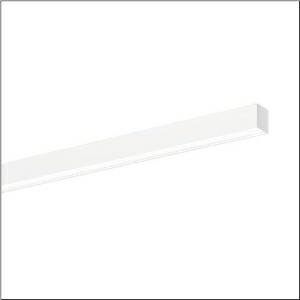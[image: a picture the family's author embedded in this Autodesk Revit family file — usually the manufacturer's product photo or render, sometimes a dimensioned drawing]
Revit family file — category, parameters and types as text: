
# Revit family: silica_r__21_51mx23db45wb_81de
name_source: partatom
category: Lighting Fixtures
units: mm (PartAtom-declared; Revit-internal decimal feet)

## family parameters
Cut with Voids When Loaded = No
Host = Face
Light Source = No
Part Type = Normal
Room Calculation Point = No
Round Connector Dimension = Use Diameter
Shared = No

## types (1)
- --- (1 x LED, 4100 lm, 28.1 W, 4000K)
    Apparent Load = 28 VA
    CIE Flux Codes = 78 96 99 100 100
    Color Rendering = 80
    Color Temperature = 4000K
    Default Elevation = 1800 mm
    Description = Silica® 21, office luminaire, primary optical cover: prismatic diffuser, of PMMA, CAT 2 (L<= 3000cd/m²), light emission: direct distribution, primary light characteristic: symmetric, installation type: surface-mounted, LED, rated luminous flux: 4.100lm, luminous efficacy: 146lm/W, light colour: 840, colour temperature: 4000K, control gear: DALI 2, with terminal, 3+2-pole, max. 2.5mm², mains connection: 220..240V, AC, 50/60Hz, rated input power: 28.1W, luminaire housing, of aluminium, traffic white (RAL 9016), length: 1.504mm, width: 53mm, height: 53mm, protection rating (complete): IP20, insulation class (complete): insulation class I (protective earthing), certification: CE, permissible operating ambient temperature: 0..+35°C, standard: EN 50419, packaging unit: 1 piece
    Height = 53 mm
    Lamp = 1 x LED
    Lamp Light Flux = 4100 lm
    Lamp Power = 28.1 W
    Lamp count = 1
    Length = 1504 mm
    Luminous efficacy = 146 lm/W
    Manufacturer = Siteco
    ModVariant = No
    Model = 51MX23DB45WB
    Mounting Place = Ceiling
    Mounting Type = Surface mounted
    Number of Poles = 1
    OnlyDefault = Yes
    Power Factor = 1
    Product Name = Silica® 21
    Product group = office luminaire | ceiling mounted
    ProductGroupID = 302
    Protection Class = Protection class I
    Protection Degree = IP 20
    RLX_Detail_Level = 1
    RLX_Emergency_Light_Flux = 0 lm
    RLX_Emergency_Type = 0
    RLX_Emergency_Type_DB = No
    RlxData = <blob elided: 18849 chars, md5=44e76a6d>
    Socket = socket
    Standby Power = 0 W
    System Light Flux = 4100 lm
    System Power = 28 W
    Type Comments = factory setting: luminous flux: 100 % | dim-lin: 254 | 323 mA
    Type Image = l_1335877.jpg
    URL = http://relux.com
    VarID = @adj_119590
    Voltage = 0 V
    Weight = 0.00 kg
    Width = 53 mm

## geometry (parser evidence)
native form markers: Blend x4, Sweep x12
no freeform markers — native parametric forms only
